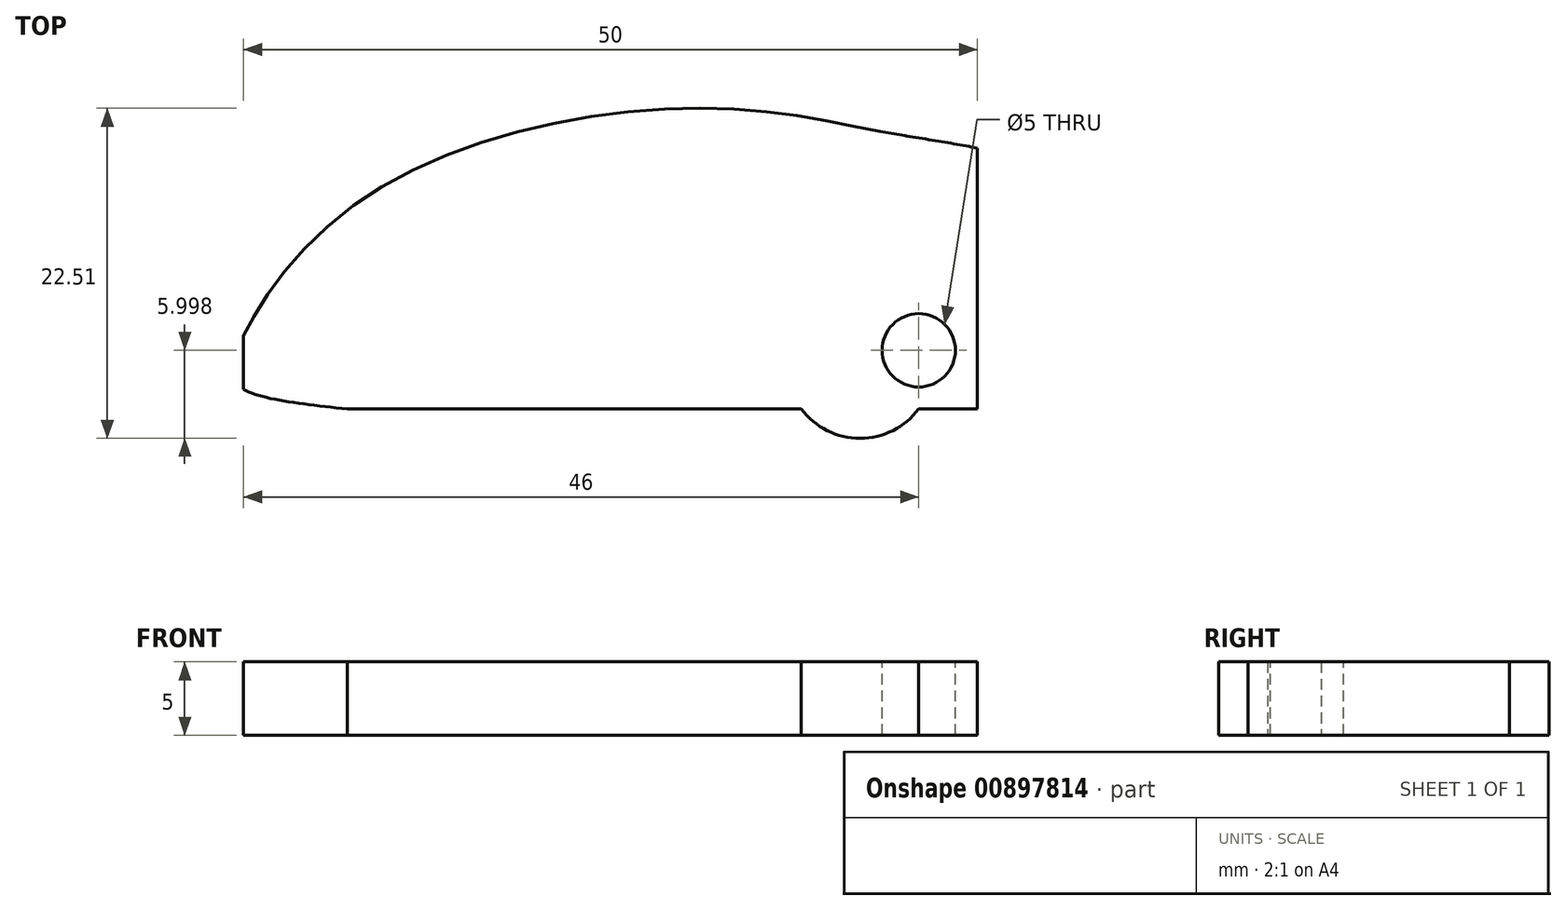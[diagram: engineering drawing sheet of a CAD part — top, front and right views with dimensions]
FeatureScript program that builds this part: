
annotation { "Feature Type Name" : "Feature", "Feature Type Description" : "" }
export const myFeature = defineFeature(function(context is Context, id is Id, definition is map)
    precondition{}
    {
        {
            var Q0;
            Q0=qCreatedBy(makeId("Top.planeOp"),FACE);
            var sketch = newSketch(context, id + "F0", { "sketchPlane" : qUnion([Q0])});
            skLineSegment(sketch, "E0.bottom", {"start": v(-10.83, 5.47) * mm, "end": v(39.17, 5.47) * mm});
            skLineSegment(sketch, "E0.top", {"start": v(-10.83, 30.47) * mm, "end": v(39.17, 30.47) * mm});
            skLineSegment(sketch, "E0.left", {"start": v(-10.83, 5.47) * mm, "end": v(-10.83, 30.47) * mm});
            skLineSegment(sketch, "E0.right", {"start": v(39.17, 5.47) * mm, "end": v(39.17, 30.47) * mm});
            skCircle(sketch, "E1", {"center": v(7.17, 8.47) * mm, "radius": 5 * mm});
            skCircle(sketch, "E2", {"center": v(31.17, 8.47) * mm, "radius": 5 * mm});
            skFitSpline(sketch, "E3", {"points": [v(39.17, 30.47) * mm, v(3.62, 30.47) * mm, v(-3.91, 27.59) * mm], "startDerivative": vector(-62.35, 3.03) * mm, "endDerivative": vector(-18.65, -10.38) * mm});
            skFitSpline(sketch, "E4", {"points": [v(-3.76, 5.47) * mm, v(-10.83, 5.47) * mm], "startDerivative": vector(-7.07, 0) * mm, "endDerivative": vector(-7.07, 0) * mm});
            skFitSpline(sketch, "E5", {"points": [v(-3.76, 5.47) * mm, v(-10.83, 6.8) * mm, v(-11.52, 8.36) * mm, v(-3.13, 19.5) * mm, v(23.55, 25.86) * mm, v(39.17, 23.82) * mm, v(52.19, 29.15) * mm], "startDerivative": vector(-67.46, 7.26) * mm, "endDerivative": vector(71.53, 41.01) * mm});
            skFitSpline(sketch, "E6", {"points": [v(34.24, 24.1) * mm, v(42.93, 22.16) * mm, v(43.86, 21.19) * mm], "startDerivative": vector(15.22, -2.42) * mm, "endDerivative": vector(2.1, -3.58) * mm});
            skSolve(sketch);
        }
        {
            var Q0;
            {var subQ4=sQuery(id+"F0.wireOp",EDGE,"E0.bottom");var subQ6=sQuery(id+"F0.wireOp",EDGE,"E1");var subQ11=makeQuery(id+"F0.imprint","INTERSECT",VERTEX,{"disambiguationData":[OD(1.0)],"derivedFrom":[subQ4,subQ6]});Q0=makeQuery(id+"F0.imprint","IMPRINT",FACE,{"disambiguationData":[TD([[makeQuery(id+"F0.imprint","IMPRINT",EDGE,{"disambiguationData":[TD([[subQ11,-1.0]])],"derivedFrom":subQ4}),1.0]])]});}
            var Q1;
            {var subQ0=sQuery(id+"F0.wireOp",EDGE,"E1");var subQ1=sQuery(id+"F0.wireOp",EDGE,"E0.bottom");var subQ2=makeQuery(id+"F0.imprint","INTERSECT",VERTEX,{"disambiguationData":[OD(0.0)],"derivedFrom":[subQ1,subQ0]});Q1=makeQuery(id+"F0.imprint","IMPRINT",FACE,{"disambiguationData":[TD([[makeQuery(id+"F0.imprint","IMPRINT",EDGE,{"disambiguationData":[TD([[subQ2,-1.0]])],"derivedFrom":subQ1}),-1.0]])]});}
            var Q2;
            {var subQ0=sQuery(id+"F0.wireOp",EDGE,"E2");var subQ1=sQuery(id+"F0.wireOp",EDGE,"E0.bottom");var subQ2=makeQuery(id+"F0.imprint","INTERSECT",VERTEX,{"disambiguationData":[OD(0.0)],"derivedFrom":[subQ1,subQ0]});Q2=makeQuery(id+"F0.imprint","IMPRINT",FACE,{"disambiguationData":[TD([[makeQuery(id+"F0.imprint","IMPRINT",EDGE,{"disambiguationData":[TD([[subQ2,-1.0]])],"derivedFrom":subQ1}),-1.0]])]});}
            var Q3;
            {var subQ0=sQuery(id+"F0.wireOp",EDGE,"E2");var subQ1=sQuery(id+"F0.wireOp",EDGE,"E0.bottom");var subQ2=makeQuery(id+"F0.imprint","INTERSECT",VERTEX,{"disambiguationData":[OD(0.0)],"derivedFrom":[subQ1,subQ0]});Q3=makeQuery(id+"F0.imprint","IMPRINT",FACE,{"disambiguationData":[TD([[makeQuery(id+"F0.imprint","IMPRINT",EDGE,{"disambiguationData":[TD([[subQ2,-1.0]])],"derivedFrom":subQ1}),1.0]])]});}
            var Q4;
            {var subQ0=sQuery(id+"F0.wireOp",EDGE,"E1");var subQ1=sQuery(id+"F0.wireOp",EDGE,"E0.bottom");var subQ2=makeQuery(id+"F0.imprint","INTERSECT",VERTEX,{"disambiguationData":[OD(0.0)],"derivedFrom":[subQ1,subQ0]});Q4=makeQuery(id+"F0.imprint","IMPRINT",FACE,{"disambiguationData":[TD([[makeQuery(id+"F0.imprint","IMPRINT",EDGE,{"disambiguationData":[TD([[subQ2,-1.0]])],"derivedFrom":subQ1}),1.0]])]});}
            var Q5;
            {var subQ0=sQuery(id+"F0.wireOp",EDGE,"E5");var subQ1=sQuery(id+"F0.wireOp",EDGE,"E0.left");var subQ2=makeQuery(id+"F0.imprint","INTERSECT",VERTEX,{"disambiguationData":[OD(0.0)],"derivedFrom":[subQ1,subQ0]});Q5=makeQuery(id+"F0.imprint","IMPRINT",FACE,{"disambiguationData":[TD([[makeQuery(id+"F0.imprint","IMPRINT",EDGE,{"disambiguationData":[TD([[subQ2,-1.0]])],"derivedFrom":subQ1}),1.0]])]});}
            extrude(context, id + "F1", {"entities" : qUnion([Q0, Q1, Q2, Q3, Q4, Q5]), "depth" : 5 * mm, "offsetDistance" : 25 * mm});
        }
        {
            var Q0;
            Q0=makeQuery(id+"F1.opExtrude","CAP_FACE",FACE,{"disambiguationData":[OSD([sQuery(id+"F0.wireOp",EDGE,"E0.bottom"),sQuery(id+"F0.wireOp",EDGE,"E0.right"),sQuery(id+"F0.wireOp",EDGE,"E1"),sQuery(id+"F0.wireOp",EDGE,"E2"),sQuery(id+"F0.wireOp",EDGE,"E5"),sQuery(id+"F0.wireOp",EDGE,"E6")])],"isStart":false});
            var sketch = newSketch(context, id + "F2", { "sketchPlane" : qUnion([Q0])});
            skCircle(sketch, "E7", {"center": v(35.17, 9.47) * mm, "radius": 2.5 * mm});
            skSolve(sketch);
        }
        {
            var Q0;
            Q0=makeQuery(id+"F2.imprint","IMPRINT",FACE,{"disambiguationData":[TD([[makeQuery(id+"F2.imprint","IMPRINT",EDGE,{"derivedFrom":sQuery(id+"F2.wireOp",EDGE,"E7")}),1.0]])]});
            extrude(context, id + "F3", {"entities" : qUnion([Q0]), "operationType" : NewBodyOperationType.REMOVE, "oppositeDirection" : true, "depth" : 25 * mm, "offsetDistance" : 25 * mm});
        }
    });
